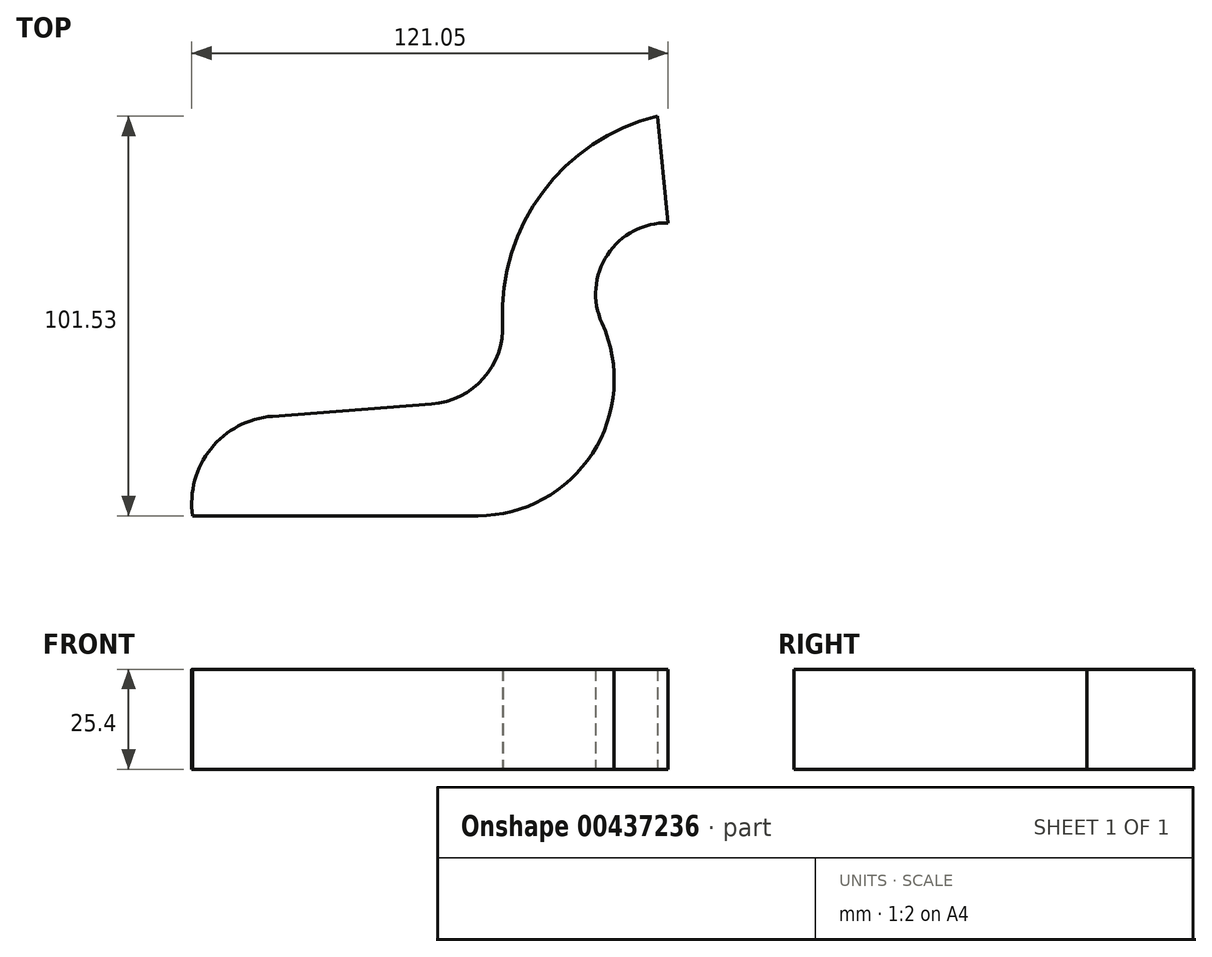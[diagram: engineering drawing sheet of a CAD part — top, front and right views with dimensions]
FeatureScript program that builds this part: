
annotation { "Feature Type Name" : "Feature", "Feature Type Description" : "" }
export const myFeature = defineFeature(function(context is Context, id is Id, definition is map)
    precondition{}
    {
        {
            var Q0;
            Q0=qCreatedBy(makeId("Top.planeOp"),FACE);
            var sketch = newSketch(context, id + "F0", { "sketchPlane" : qUnion([Q0])});
            skArc(sketch, "E0", {"start": v(-60.66, -48.93) * mm, "mid": v(-56.02, -31.89) * mm, "end": v(-40.4, -23.64) * mm});
            skLineSegment(sketch, "E1", {"start": v(-40.4, -23.64) * mm, "end": v(0, -20.55) * mm});
            skArc(sketch, "E2", {"start": v(0, -20.55) * mm, "mid": v(13.24, -13.96) * mm, "end": v(18.13, 0) * mm});
            skArc(sketch, "E3", {"start": v(18.13, 0) * mm, "mid": v(28.32, 33.36) * mm, "end": v(57.42, 52.6) * mm});
            skLineSegment(sketch, "E4", {"start": v(-60.66, -48.93) * mm, "end": v(-60.66, -48.93) * mm});
            skLineSegment(sketch, "E5", {"start": v(-60.66, -48.93) * mm, "end": v(11.82, -48.93) * mm});
            skArc(sketch, "E6", {"start": v(11.82, -48.93) * mm, "mid": v(40.92, -33.06) * mm, "end": v(43.35, 0) * mm});
            skArc(sketch, "E7", {"start": v(43.35, 0) * mm, "mid": v(44.71, 17.39) * mm, "end": v(60.16, 25.5) * mm});
            skLineSegment(sketch, "E8", {"start": v(60.16, 25.5) * mm, "end": v(57.42, 52.6) * mm});
            skSolve(sketch);
        }
        {
            var Q0;
            Q0=sQuery(id+"F0.wireOp",EDGE,"E2");
            var Q1;
            Q1=sQuery(id+"F0.wireOp",EDGE,"E1");
            var Q2;
            Q2=sQuery(id+"F0.wireOp",EDGE,"E0");
            var Q3;
            Q3=sQuery(id+"F0.wireOp",EDGE,"E3");
            extrude(context, id + "F1", {"bodyType" : ToolBodyType.SURFACE, "surfaceEntities" : qUnion([Q0, Q1, Q2, Q3]), "oppositeDirection" : true, "depth" : 25.4 * mm, "offsetDistance" : 25.4 * mm});
        }
        {
            var Q0;
            Q0=sQuery(id+"F0.wireOp",EDGE,"E5");
            var Q1;
            Q1=sQuery(id+"F0.wireOp",EDGE,"E6");
            var Q2;
            Q2=sQuery(id+"F0.wireOp",EDGE,"E7");
            extrude(context, id + "F2", {"bodyType" : ToolBodyType.SURFACE, "surfaceEntities" : qUnion([Q0, Q1, Q2]), "oppositeDirection" : true, "depth" : 25.4 * mm, "offsetDistance" : 25.4 * mm});
        }
        {
            var Q0;
            Q0=sQuery(id+"F0.wireOp",EDGE,"E8");
            extrude(context, id + "F3", {"bodyType" : ToolBodyType.SURFACE, "surfaceEntities" : qUnion([Q0]), "oppositeDirection" : true, "depth" : 25.4 * mm, "offsetDistance" : 25.4 * mm});
        }
    });
